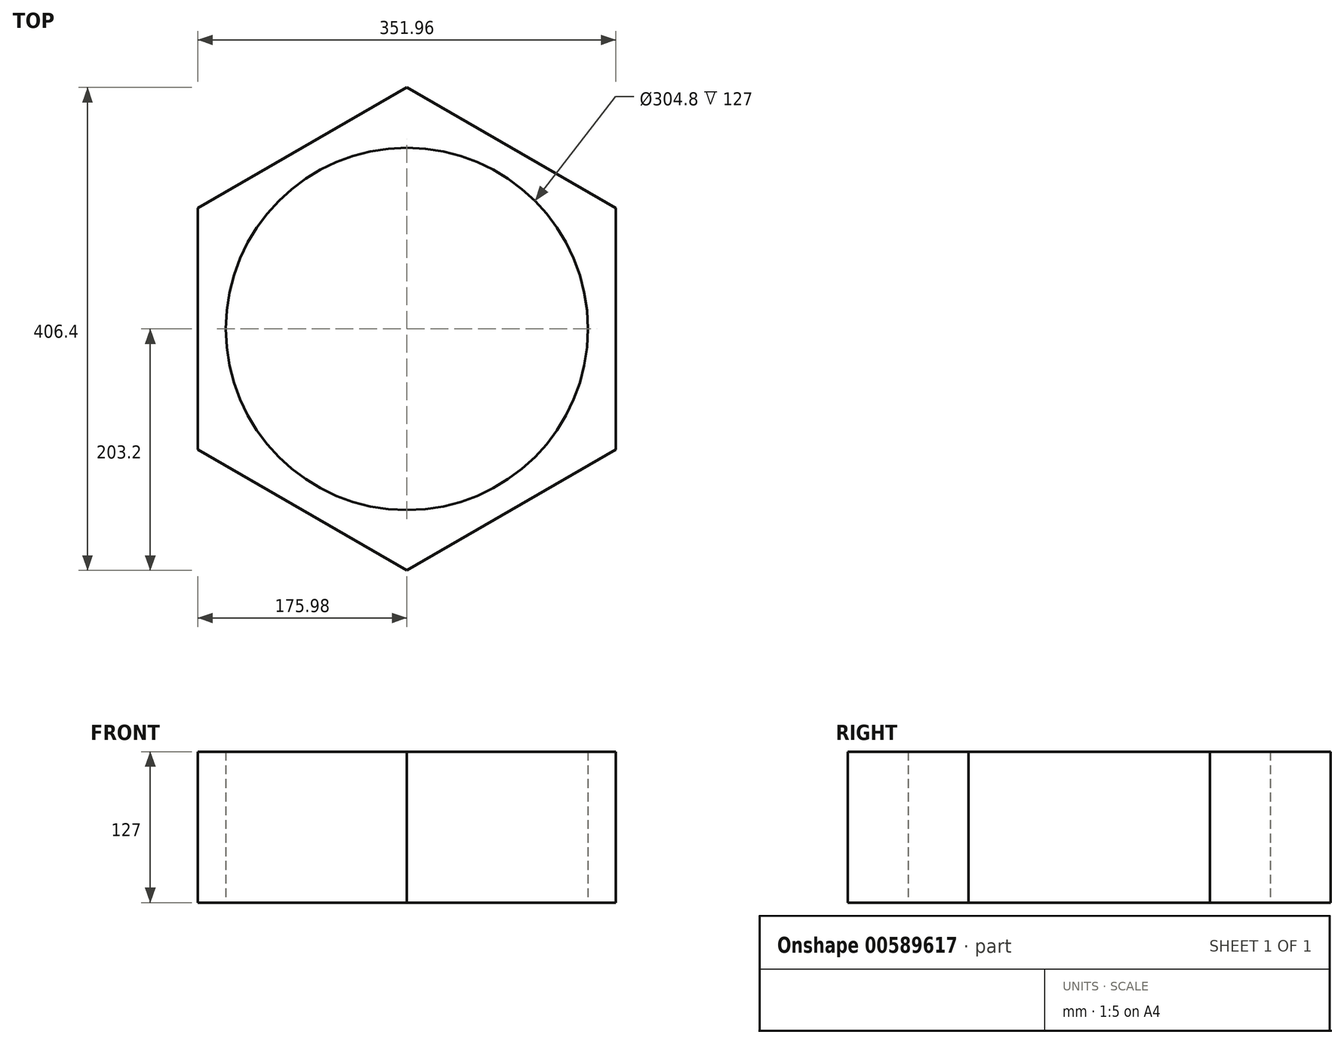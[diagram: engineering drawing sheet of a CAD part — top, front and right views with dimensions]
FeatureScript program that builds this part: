
annotation { "Feature Type Name" : "Feature", "Feature Type Description" : "" }
export const myFeature = defineFeature(function(context is Context, id is Id, definition is map)
    precondition{}
    {
        {
            var Q0;
            Q0=qCreatedBy(makeId("Top.planeOp"),FACE);
            var sketch = newSketch(context, id + "F0", { "sketchPlane" : qUnion([Q0])});
            skCircle(sketch, "E0.cCircle", {"center": v(0, 0) * mm, "radius": 175.98 * mm, "construction": true});
            skLineSegment(sketch, "E0.0", {"start": v(175.98, 101.6) * mm, "end": v(175.98, -101.6) * mm});
            skLineSegment(sketch, "E0.1", {"start": v(175.98, -101.6) * mm, "end": v(0, -203.2) * mm});
            skLineSegment(sketch, "E0.2", {"start": v(0, -203.2) * mm, "end": v(-175.98, -101.6) * mm});
            skLineSegment(sketch, "E0.3", {"start": v(-175.98, -101.6) * mm, "end": v(-175.98, 101.6) * mm});
            skLineSegment(sketch, "E0.4", {"start": v(-175.98, 101.6) * mm, "end": v(0, 203.2) * mm});
            skLineSegment(sketch, "E0.5", {"start": v(0, 203.2) * mm, "end": v(175.98, 101.6) * mm});
            skPoint(sketch, "E0.0.midPoint", {"position": v(175.98, 0) * mm});
            skCircle(sketch, "E1", {"center": v(0, 0) * mm, "radius": 152.4 * mm});
            skSolve(sketch);
        }
        {
            var Q0;
            Q0=makeQuery(id+"F0.imprint","IMPRINT",FACE,{"disambiguationData":[TD([[makeQuery(id+"F0.imprint","IMPRINT",EDGE,{"derivedFrom":sQuery(id+"F0.wireOp",EDGE,"E0.0")}),-1.0]])]});
            extrude(context, id + "F1", {"entities" : qUnion([Q0]), "depth" : 127 * mm, "offsetDistance" : 25.4 * mm});
        }
    });
